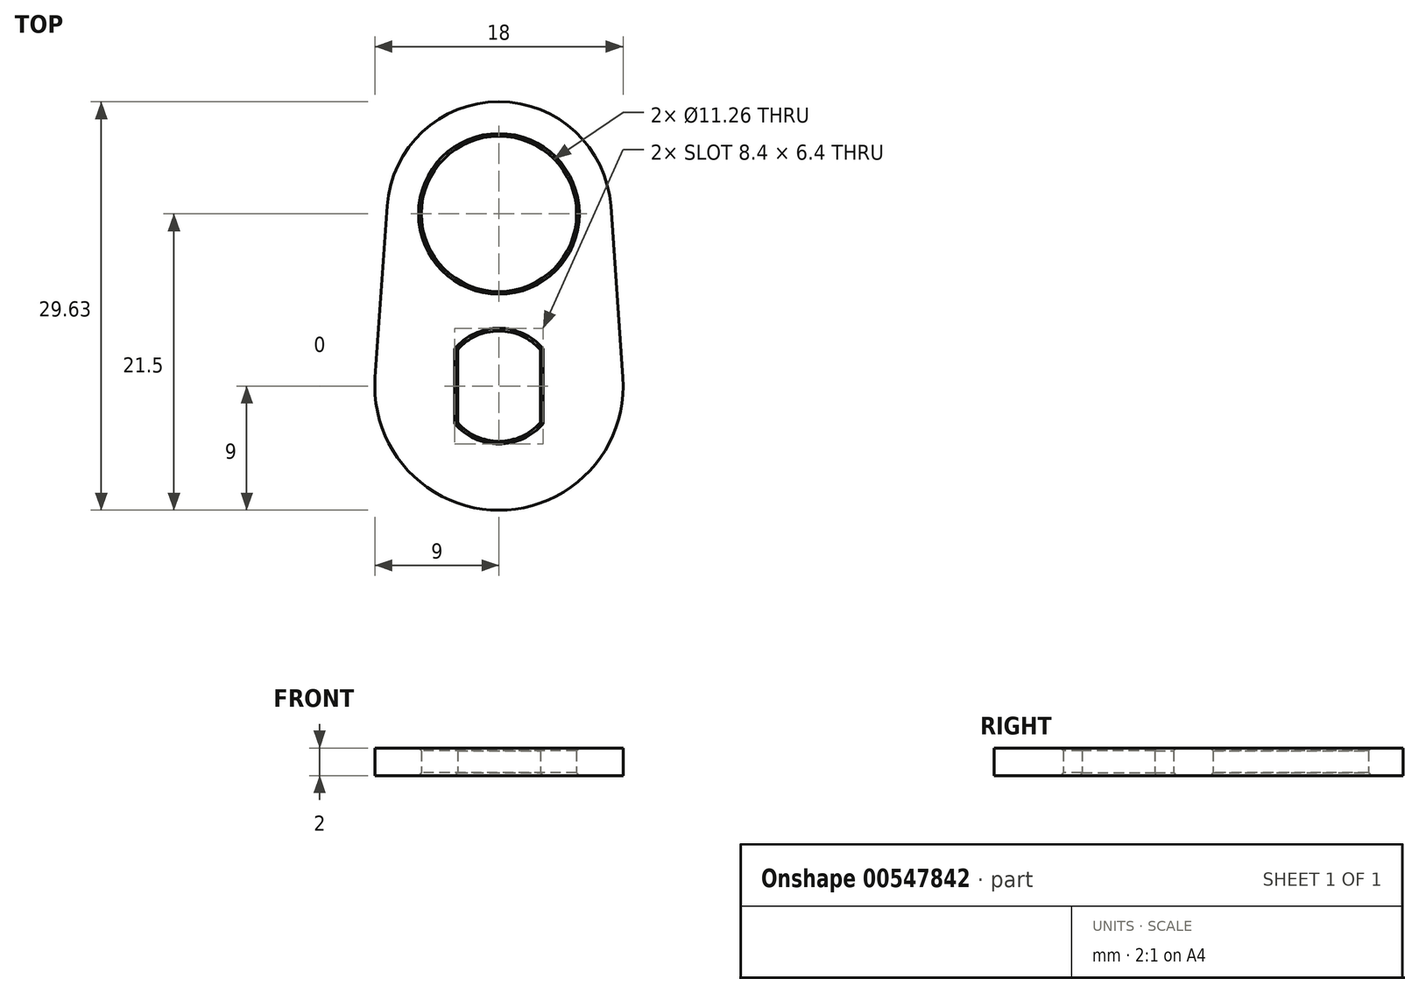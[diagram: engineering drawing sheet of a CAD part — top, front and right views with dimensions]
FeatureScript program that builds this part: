
annotation { "Feature Type Name" : "Feature", "Feature Type Description" : "" }
export const myFeature = defineFeature(function(context is Context, id is Id, definition is map)
    precondition{}
    {
        {
            var Q0;
            Q0=qCreatedBy(makeId("Top.planeOp"),FACE);
            var sketch = newSketch(context, id + "F0", { "sketchPlane" : qUnion([Q0])});
            skArc(sketch, "E0", {"start": v(-8.98, 0.63) * mm, "mid": v(0, -9) * mm, "end": v(8.98, 0.63) * mm});
            skArc(sketch, "E1", {"start": v(8.11, 13.07) * mm, "mid": v(0, 20.63) * mm, "end": v(-8.11, 13.07) * mm});
            skArc(sketch, "E2", {"start": v(-3, -2.65) * mm, "mid": v(0, -4) * mm, "end": v(3, -2.65) * mm});
            skLineSegment(sketch, "E3", {"start": v(-8.11, 13.07) * mm, "end": v(-8.98, 0.63) * mm});
            skLineSegment(sketch, "E4", {"start": v(8.11, 13.07) * mm, "end": v(8.98, 0.63) * mm});
            skCircle(sketch, "E5", {"center": v(0, 12.5) * mm, "radius": 5.63 * mm});
            skLineSegment(sketch, "E6", {"start": v(-3, 2.65) * mm, "end": v(-3, -2.65) * mm});
            skLineSegment(sketch, "E7.MirrorCS", {"start": v(3, 2.65) * mm, "end": v(3, -2.65) * mm});
            skArc(sketch, "E8.trimOffspring", {"start": v(3, 2.65) * mm, "mid": v(0, 4) * mm, "end": v(-3, 2.65) * mm});
            skSolve(sketch);
        }
        {
            var Q0;
            Q0=makeQuery(id+"F0.imprint","IMPRINT",FACE,{"disambiguationData":[TD([[makeQuery(id+"F0.imprint","IMPRINT",EDGE,{"derivedFrom":sQuery(id+"F0.wireOp",EDGE,"E0")}),1.0]])]});
            extrude(context, id + "F1", {"entities" : qUnion([Q0]), "depth" : 2 * mm, "offsetDistance" : 25 * mm});
        }
        {
            var Q0;
            Q0=makeQuery(id+"F1.opExtrude","CAP_EDGE",EDGE,{"disambiguationData":[OSD([sQuery(id+"F0.wireOp",EDGE,"E6")])],"isStart":false});
            var Q1;
            Q1=makeQuery(id+"F1.opExtrude","CAP_EDGE",EDGE,{"disambiguationData":[OSD([sQuery(id+"F0.wireOp",EDGE,"E2")])],"isStart":false});
            var Q2;
            Q2=makeQuery(id+"F1.opExtrude","CAP_EDGE",EDGE,{"disambiguationData":[OSD([sQuery(id+"F0.wireOp",EDGE,"E7.MirrorCS")])],"isStart":false});
            var Q3;
            Q3=makeQuery(id+"F1.opExtrude","CAP_EDGE",EDGE,{"disambiguationData":[OSD([sQuery(id+"F0.wireOp",EDGE,"E8.trimOffspring")])],"isStart":false});
            var Q4;
            Q4=makeQuery(id+"F1.opExtrude","CAP_EDGE",EDGE,{"disambiguationData":[OSD([sQuery(id+"F0.wireOp",EDGE,"E7.MirrorCS")])],"isStart":true});
            var Q5;
            Q5=makeQuery(id+"F1.opExtrude","CAP_EDGE",EDGE,{"disambiguationData":[OSD([sQuery(id+"F0.wireOp",EDGE,"E2")])],"isStart":true});
            var Q6;
            Q6=makeQuery(id+"F1.opExtrude","CAP_EDGE",EDGE,{"disambiguationData":[OSD([sQuery(id+"F0.wireOp",EDGE,"E8.trimOffspring")])],"isStart":true});
            var Q7;
            Q7=makeQuery(id+"F1.opExtrude","CAP_EDGE",EDGE,{"disambiguationData":[OSD([sQuery(id+"F0.wireOp",EDGE,"E6")])],"isStart":true});
            var Q8;
            Q8=makeQuery(id+"F1.opExtrude","CAP_EDGE",EDGE,{"disambiguationData":[OSD([sQuery(id+"F0.wireOp",EDGE,"E5")])],"isStart":false});
            var Q9;
            Q9=makeQuery(id+"F1.opExtrude","CAP_EDGE",EDGE,{"disambiguationData":[OSD([sQuery(id+"F0.wireOp",EDGE,"E5")])],"isStart":true});
            chamfer(context, id + "F2", {"entities" : qUnion([Q0, Q1, Q2, Q3, Q4, Q5, Q6, Q7, Q8, Q9]), "chamferType" : ChamferType.OFFSET_ANGLE, "width" : 0.2 * mm, "oppositeDirection" : false, "angle" : 45 * degree, "tangentPropagation" : true});
        }
    });
